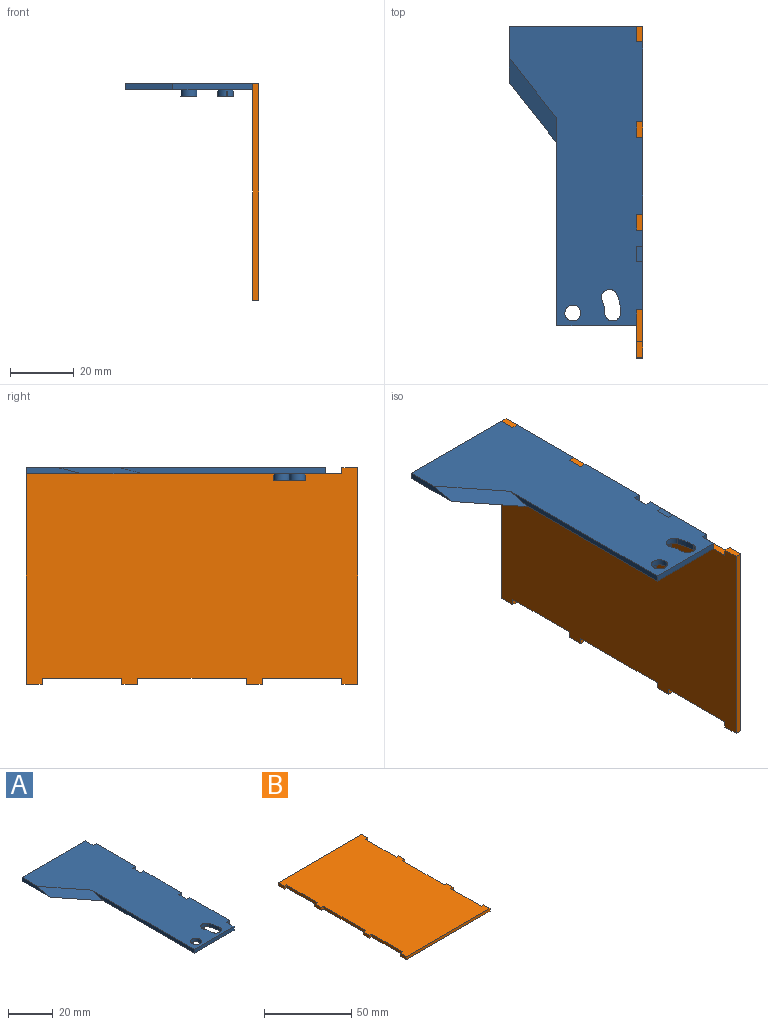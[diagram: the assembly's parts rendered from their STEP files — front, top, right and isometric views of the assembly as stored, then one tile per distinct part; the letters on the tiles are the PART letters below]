
ASSEMBLY  parts=2 mates=1
PART A: 30 faces, bbox 42x94x4 mm
  f0: plane 94x42mm, normal (0,0,1), area 2725.1mm2, adj f2,f3,f4,f5,f6,f7,f8,f9
  f1: plane 94x42mm, normal (0,0,-1), area 2802.7mm2, adj f2,f3,f4,f5,f6,f7,f8,f9
  f2: plane 65.07x2mm, normal (-1,0,0), area 122.3mm2, adj f0,f1,f3,f29
  f3: plane 25x2mm, normal (0,-1,0), area 50mm2, adj f0,f1,f2,f4
  f4: plane 5x2mm, normal (1,0,0), area 10mm2, adj f0,f1,f3,f5
  f5: plane 2x2mm, normal (0,-1,0), area 4mm2, adj f0,f1,f4,f6
  f6: plane 25x2mm, normal (1,0,0), area 50mm2, adj f0,f1,f5,f7
  f7: plane 2x2mm, normal (0,1,0), area 4mm2, adj f0,f1,f6,f8
  f8: plane 5x2mm, normal (1,0,0), area 10mm2, adj f0,f1,f7,f9
  f9: plane 2x2mm, normal (0,-1,0), area 4mm2, adj f0,f1,f8,f10
  f10: plane 24x2mm, normal (1,0,0), area 48mm2, adj f0,f1,f9,f11
  f11: plane 2x2mm, normal (0,1,0), area 4mm2, adj f0,f1,f10,f12
  f12: plane 5x2mm, normal (1,0,0), area 10mm2, adj f0,f1,f11,f13
  f13: plane 2x2mm, normal (0,-1,0), area 4mm2, adj f0,f1,f12,f14
  f14: plane 25x2mm, normal (1,0,0), area 50mm2, adj f0,f1,f13,f15
  f15: plane 2x2mm, normal (0,1,0), area 4mm2, adj f0,f1,f14,f16
  f16: plane 5x2mm, normal (1,0,0), area 10mm2, adj f0,f1,f15,f17
  f17: plane 40x2mm, normal (0,1,0), area 80mm2, adj f0,f1,f16,f18
  f18: plane 17.72x2mm, normal (-1,0,0), area 27.7mm2, adj f0,f1,f17,f29
  f19: cylinder r=2.5mm len=5mm, axis (0,0,1), area 31.4mm2, adj f1,f20
  f20: plane 5x5mm, normal (0,0,-1), area 19.6mm2, adj f19
  f21: cylinder r=2.5mm len=5mm, axis (0,0,1), area 30.6mm2, adj f1,f22,f23
  f22: cylinder r=2.5mm len=2mm, axis (0,0,1), area 0.8mm2, adj f1,f21,f23
  f23: plane 5x5mm, normal (0,0,-1), area 19.6mm2, adj f21,f22
  f24: cylinder r=10mm len=3.91mm, axis (0,0,-1), area 8mm2, adj f0,f1,f25,f27
  f25: cylinder r=2.5mm len=5mm, axis (0,0,-1), area 15.7mm2, adj f0,f1,f24,f26
  f26: cylinder r=15mm len=5.86mm, axis (0,0,-1), area 12mm2, adj f0,f1,f25,f27
  f27: cylinder r=2.5mm len=4.8mm, axis (0,0,-1), area 15.7mm2, adj f0,f1,f24,f26
  f28: cylinder r=2.5mm len=5mm, axis (0,0,-1), area 31.4mm2, adj f0,f1
  f29: plane 26.79x15mm, normal (-0.3,-0.24,0.92), area 126.5mm2, adj f0,f1,f2,f18
PART B: 30 faces, bbox 68x104x2 mm
  f0: plane 68x2mm, normal (0,1,0), area 136mm2, adj f1,f27,f28,f29
  f1: plane 5x2mm, normal (-1,0,0), area 10mm2, adj f0,f2,f28,f29
  f2: plane 2x2mm, normal (0,-1,0), area 4mm2, adj f1,f3,f28,f29
  f3: plane 25x2mm, normal (-1,0,0), area 50mm2, adj f2,f4,f28,f29
  f4: plane 2x2mm, normal (0,1,0), area 4mm2, adj f3,f5,f28,f29
  f5: plane 5x2mm, normal (-1,0,0), area 10mm2, adj f4,f6,f28,f29
  f6: plane 2x2mm, normal (0,-1,0), area 4mm2, adj f5,f7,f28,f29
  f7: plane 34x2mm, normal (-1,0,0), area 68mm2, adj f6,f8,f28,f29
  f8: plane 2x2mm, normal (0,1,0), area 4mm2, adj f7,f9,f28,f29
  f9: plane 5x2mm, normal (-1,0,0), area 10mm2, adj f8,f10,f28,f29
  f10: plane 2x2mm, normal (0,-1,0), area 4mm2, adj f9,f11,f28,f29
  f11: plane 25x2mm, normal (-1,0,0), area 50mm2, adj f10,f12,f28,f29
  f12: plane 2x2mm, normal (0,1,0), area 4mm2, adj f11,f13,f28,f29
  f13: plane 5x2mm, normal (-1,0,0), area 10mm2, adj f12,f14,f28,f29
  f14: plane 68x2mm, normal (0,-1,0), area 136mm2, adj f13,f15,f28,f29
  f15: plane 5x2mm, normal (1,0,0), area 10mm2, adj f14,f16,f28,f29
  f16: plane 2x2mm, normal (0,1,0), area 4mm2, adj f15,f17,f28,f29
  f17: plane 25x2mm, normal (1,0,0), area 50mm2, adj f16,f18,f28,f29
  f18: plane 2x2mm, normal (0,-1,0), area 4mm2, adj f17,f19,f28,f29
  f19: plane 5x2mm, normal (1,0,0), area 10mm2, adj f18,f20,f28,f29
  f20: plane 2x2mm, normal (0,1,0), area 4mm2, adj f19,f21,f28,f29
  f21: plane 34x2mm, normal (1,0,0), area 68mm2, adj f20,f22,f28,f29
  f22: plane 2x2mm, normal (0,-1,0), area 4mm2, adj f21,f23,f28,f29
  f23: plane 5x2mm, normal (1,0,0), area 10mm2, adj f22,f24,f28,f29
  f24: plane 2x2mm, normal (0,1,0), area 4mm2, adj f23,f25,f28,f29
  f25: plane 25x2mm, normal (1,0,0), area 50mm2, adj f24,f26,f28,f29
  f26: plane 2x2mm, normal (0,-1,0), area 4mm2, adj f25,f27,f28,f29
  f27: plane 5x2mm, normal (1,0,0), area 10mm2, adj f0,f26,f28,f29
  f28: plane 104x68mm, normal (0,0,1), area 6736mm2, adj f0,f1,f2,f3,f4,f5,f6,f7
  f29: plane 104x68mm, normal (0,0,-1), area 6736mm2, adj f0,f1,f2,f3,f4,f5,f6,f7
PLACE A t=(-5.7,-49.51,0)mm
PLACE B rot(axis=(0,1,0),90deg) t=(14.3,-17.73,-35.18)mm
MATE fastened B.f29 <-> A.f16  axis (-1,0,0) through (14.3,35.49,2)mm
